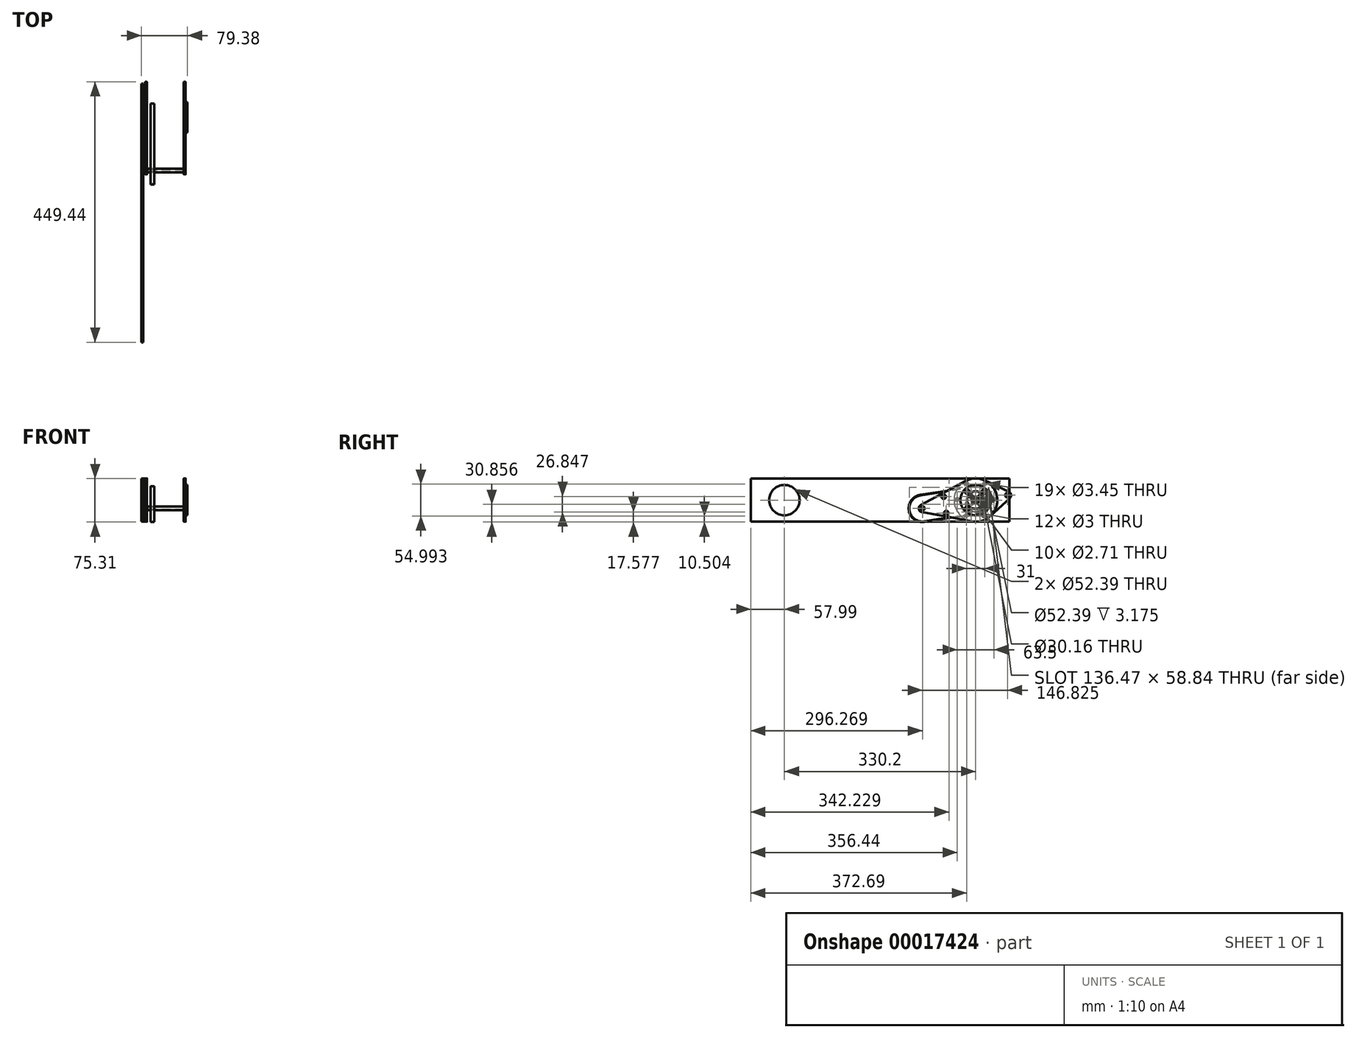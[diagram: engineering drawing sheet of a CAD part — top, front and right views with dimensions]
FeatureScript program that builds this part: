
annotation { "Feature Type Name" : "Feature", "Feature Type Description" : "" }
export const myFeature = defineFeature(function(context is Context, id is Id, definition is map)
    precondition{}
    {
        {
            var Q0;
            Q0=qCreatedBy(makeId("Right.planeOp"),FACE);
            var sketch = newSketch(context, id + "F0", { "sketchPlane" : qUnion([Q0])});
            skCircle(sketch, "E0", {"center": v(0, 0) * mm, "radius": 50.8 * mm, "construction": true});
            skCircle(sketch, "E1", {"center": v(-91.92, -14.29) * mm, "radius": 36.51 * mm, "construction": true});
            skLineSegment(sketch, "E2", {"start": v(0, 0) * mm, "end": v(-91.92, -14.29) * mm, "construction": true});
            skCircle(sketch, "E3", {"center": v(0, -7) * mm, "radius": 18.5 * mm, "construction": true});
            skCircle(sketch, "E4", {"center": v(0, 0) * mm, "radius": 6 * mm});
            skCircle(sketch, "E5", {"center": v(0, 0) * mm, "radius": 26.2 * mm, "construction": true});
            skLineSegment(sketch, "E6", {"start": v(63.5, -50.8) * mm, "end": v(-393.7, -50.8) * mm});
            skLineSegment(sketch, "E7", {"start": v(-165.1, -50.8) * mm, "end": v(-165.1, 406.4) * mm, "construction": true});
            skCircle(sketch, "E8.MirrorC", {"center": v(-238.28, -14.29) * mm, "radius": 36.51 * mm});
            skLineSegment(sketch, "E9.MirrorCS", {"start": v(-330.2, 0) * mm, "end": v(-238.28, -14.29) * mm, "construction": true});
            skCircle(sketch, "E10.MirrorC", {"center": v(-330.2, 0) * mm, "radius": 50.8 * mm});
            skArc(sketch, "E11", {"start": v(-6.86, -36.67) * mm, "mid": v(10.31, -35.85) * mm, "end": v(25.3, -27.42) * mm});
            skArc(sketch, "E12", {"start": v(59.2, 3.87) * mm, "mid": v(61.18, 9.5) * mm, "end": v(57.59, 14.29) * mm});
            skArc(sketch, "E13", {"start": v(-94.93, -8.7) * mm, "mid": v(-98.2, -15.26) * mm, "end": v(-93.09, -20.53) * mm});
            skLineSegment(sketch, "E14", {"start": v(15.78, 33.8) * mm, "end": v(57.59, 14.29) * mm});
            skLineSegment(sketch, "E15", {"start": v(59.2, 3.87) * mm, "end": v(25.3, -27.42) * mm});
            skLineSegment(sketch, "E16", {"start": v(-93.09, -20.53) * mm, "end": v(-6.86, -36.67) * mm});
            skLineSegment(sketch, "E17", {"start": v(-94.93, -8.7) * mm, "end": v(-17.67, 32.86) * mm});
            skArc(sketch, "E18.trimOffspring", {"start": v(15.78, 33.8) * mm, "mid": v(-1.06, 37.3) * mm, "end": v(-17.67, 32.86) * mm});
            skCircle(sketch, "E19", {"center": v(54.9, 8.53) * mm, "radius": 3.18 * mm, "construction": true});
            skCircle(sketch, "E20", {"center": v(-91.92, -14.29) * mm, "radius": 3.18 * mm, "construction": true});
            skSolve(sketch);
        }
        {
            var Q0;
            Q0=makeQuery(id+"F0.imprint","IMPRINT",FACE,{"disambiguationData":[TD([[makeQuery(id+"F0.imprint","IMPRINT",EDGE,{"derivedFrom":sQuery(id+"F0.wireOp",EDGE,"E4")}),-1.0]])]});
            extrude(context, id + "F1", {"entities" : qUnion([Q0]), "depth" : 3.17 * mm});
        }
        {
            var Q0;
            Q0=makeQuery(id+"F0.imprint","IMPRINT",FACE,{"disambiguationData":[TD([[makeQuery(id+"F0.imprint","IMPRINT",EDGE,{"derivedFrom":sQuery(id+"F0.wireOp",EDGE,"E4")}),-1.0]])]});
            var sketch = newSketch(context, id + "F2", { "sketchPlane" : qUnion([Q0])});
            skCircle(sketch, "E21.0", {"center": v(0, 0) * mm, "radius": 26.2 * mm});
            skCircle(sketch, "E22.cCircle", {"center": v(0, 0) * mm, "radius": 20.64 * mm, "construction": true});
            skLineSegment(sketch, "E22.0", {"start": v(-14.6, -14.6) * mm, "end": v(-14.6, 14.6) * mm, "construction": true});
            skLineSegment(sketch, "E22.1", {"start": v(-14.6, 14.6) * mm, "end": v(14.6, 14.6) * mm, "construction": true});
            skLineSegment(sketch, "E22.2", {"start": v(14.6, 14.6) * mm, "end": v(14.6, -14.6) * mm, "construction": true});
            skLineSegment(sketch, "E22.3", {"start": v(14.6, -14.6) * mm, "end": v(-14.6, -14.6) * mm, "construction": true});
            skCircle(sketch, "E23", {"center": v(-14.6, -14.6) * mm, "radius": 3.9 * mm});
            skCircle(sketch, "E24.0", {"center": v(0, 0) * mm, "radius": 6 * mm});
            skSolve(sketch);
        }
        {
            var Q0;
            Q0=makeQuery(id+"F2.imprint","IMPRINT",FACE,{"disambiguationData":[TD([[makeQuery(id+"F2.imprint","IMPRINT",EDGE,{"derivedFrom":sQuery(id+"F2.wireOp",EDGE,"E21.0")}),1.0]])]});
            var Q1;
            Q1=makeQuery(id+"F2.imprint","IMPRINT",FACE,{"disambiguationData":[TD([[makeQuery(id+"F2.imprint","IMPRINT",EDGE,{"derivedFrom":sQuery(id+"F2.wireOp",EDGE,"E23")}),1.0]])]});
            extrude(context, id + "F3", {"entities" : qUnion([Q0, Q1]), "oppositeDirection" : true, "depth" : 3.17 * mm});
        }
        {
            var Q0;
            Q0=makeQuery(id+"F3.opExtrude","CAP_FACE",FACE,{"disambiguationData":[OSD([sQuery(id+"F2.wireOp",EDGE,"E21.0"),sQuery(id+"F2.wireOp",EDGE,"E24.0")])],"isStart":false});
            var sketch = newSketch(context, id + "F4", { "sketchPlane" : qUnion([Q0])});
            skPoint(sketch, "E25.0", {"position": v(14.6, 14.6) * mm});
            skPoint(sketch, "E25.1", {"position": v(-14.6, 14.6) * mm});
            skPoint(sketch, "E25.2", {"position": v(-14.6, -14.6) * mm});
            skPoint(sketch, "E25.3", {"position": v(14.6, -14.6) * mm});
            skSolve(sketch);
        }
        {
            var Q0;
            Q0=sQuery(id+"F4.wireOp",VERTEX,"E25.3");
            var Q1;
            Q1=sQuery(id+"F4.wireOp",VERTEX,"E25.0");
            var Q2;
            Q2=sQuery(id+"F4.wireOp",VERTEX,"E25.1");
            var Q3;
            Q3=sQuery(id+"F4.wireOp",VERTEX,"E25.2");
            var Q4;
            Q4=makeQuery(id+"F3.opExtrude","SWEPT_BODY",BODY,{"disambiguationData":[OSD([sQuery(id+"F2.wireOp",EDGE,"E21.0"),sQuery(id+"F2.wireOp",EDGE,"E24.0")])]});
            hole(context, id + "F5", {"style" : HoleStyle.C_SINK, "holeDiameter" : 3.45 * mm, "cSinkDiameter" : 7.8 * mm, "endStyle" : HoleEndStyle.THROUGH, "locations" : qUnion([Q0, Q1, Q2, Q3]), "scope" : qUnion([Q4]), "cSinkAngle" : 90 * degree});
        }
        {
            var Q0;
            Q0=makeQuery(id+"F1.opExtrude","CAP_FACE",FACE,{"disambiguationData":[OSD([sQuery(id+"F0.wireOp",EDGE,"E4"),sQuery(id+"F0.wireOp",EDGE,"E11"),sQuery(id+"F0.wireOp",EDGE,"E12"),sQuery(id+"F0.wireOp",EDGE,"E13"),sQuery(id+"F0.wireOp",EDGE,"E14"),sQuery(id+"F0.wireOp",EDGE,"E15"),sQuery(id+"F0.wireOp",EDGE,"E16"),sQuery(id+"F0.wireOp",EDGE,"E17"),sQuery(id+"F0.wireOp",EDGE,"E18.trimOffspring")])],"isStart":false});
            var sketch = newSketch(context, id + "F6", { "sketchPlane" : qUnion([Q0])});
            skPoint(sketch, "E26.0", {"position": v(0, -7) * mm});
            skCircle(sketch, "E27.cCircle", {"center": v(0, -7) * mm, "radius": 15.5 * mm, "construction": true});
            skLineSegment(sketch, "E27.0", {"start": v(15.5, -7) * mm, "end": v(7.75, -20.42) * mm});
            skLineSegment(sketch, "E27.1", {"start": v(7.75, -20.42) * mm, "end": v(-7.75, -20.42) * mm});
            skLineSegment(sketch, "E27.2", {"start": v(-7.75, -20.42) * mm, "end": v(-15.5, -7) * mm});
            skLineSegment(sketch, "E27.3", {"start": v(-15.5, -7) * mm, "end": v(-7.75, 6.42) * mm});
            skLineSegment(sketch, "E27.4", {"start": v(-7.75, 6.42) * mm, "end": v(7.75, 6.42) * mm});
            skLineSegment(sketch, "E27.5", {"start": v(7.75, 6.42) * mm, "end": v(15.5, -7) * mm});
            skSolve(sketch);
        }
        {
            var Q0;
            Q0=sQuery(id+"F6.wireOp",VERTEX,"E27.3.end");
            var Q1;
            Q1=sQuery(id+"F6.wireOp",VERTEX,"E27.2.end");
            var Q2;
            Q2=sQuery(id+"F6.wireOp",VERTEX,"E27.2.start");
            var Q3;
            Q3=sQuery(id+"F6.wireOp",VERTEX,"E27.0.end");
            var Q4;
            Q4=sQuery(id+"F6.wireOp",VERTEX,"E27.0.start");
            var Q5;
            Q5=sQuery(id+"F6.wireOp",VERTEX,"E27.4.end");
            var Q6;
            Q6=makeQuery(id+"F1.opExtrude","SWEPT_BODY",BODY,{"disambiguationData":[OSD([sQuery(id+"F0.wireOp",EDGE,"E4"),sQuery(id+"F0.wireOp",EDGE,"E11"),sQuery(id+"F0.wireOp",EDGE,"E12"),sQuery(id+"F0.wireOp",EDGE,"E13"),sQuery(id+"F0.wireOp",EDGE,"E14"),sQuery(id+"F0.wireOp",EDGE,"E15"),sQuery(id+"F0.wireOp",EDGE,"E16"),sQuery(id+"F0.wireOp",EDGE,"E17"),sQuery(id+"F0.wireOp",EDGE,"E18.trimOffspring")])]});
            var Q7;
            Q7=makeQuery(id+"F3.opExtrude","SWEPT_BODY",BODY,{"disambiguationData":[OSD([sQuery(id+"F2.wireOp",EDGE,"E21.0"),sQuery(id+"F2.wireOp",EDGE,"E24.0")])]});
            hole(context, id + "F7", {"style" : HoleStyle.C_SINK, "holeDiameter" : 3 * mm, "cSinkDiameter" : 6 * mm, "endStyle" : HoleEndStyle.THROUGH, "locations" : qUnion([Q0, Q1, Q2, Q3, Q4, Q5]), "scope" : qUnion([Q6, Q7]), "cSinkAngle" : 90 * degree});
        }
        {
            var Q0;
            Q0=makeQuery(id+"F2.imprint","IMPRINT",FACE,{"disambiguationData":[TD([[makeQuery(id+"F2.imprint","IMPRINT",EDGE,{"derivedFrom":sQuery(id+"F2.wireOp",EDGE,"E21.0")}),-1.0]])]});
            var sketch = newSketch(context, id + "F8", { "sketchPlane" : qUnion([Q0])});
            skCircle(sketch, "E28", {"center": v(0, 0) * mm, "radius": 37.3 * mm});
            skCircle(sketch, "E29.cCircle", {"center": v(0, 0) * mm, "radius": 31.75 * mm, "construction": true});
            skLineSegment(sketch, "E29.0", {"start": v(-31.75, 0) * mm, "end": v(-15.88, 27.5) * mm, "construction": true});
            skLineSegment(sketch, "E29.1", {"start": v(-15.87, 27.5) * mm, "end": v(15.87, 27.5) * mm, "construction": true});
            skLineSegment(sketch, "E29.2", {"start": v(15.88, 27.5) * mm, "end": v(31.75, 0) * mm, "construction": true});
            skLineSegment(sketch, "E29.3", {"start": v(31.75, 0) * mm, "end": v(15.87, -27.5) * mm, "construction": true});
            skLineSegment(sketch, "E29.4", {"start": v(15.88, -27.5) * mm, "end": v(-15.88, -27.5) * mm, "construction": true});
            skLineSegment(sketch, "E29.5", {"start": v(-15.88, -27.5) * mm, "end": v(-31.75, 0) * mm, "construction": true});
            skCircle(sketch, "E30", {"center": v(-31.75, 0) * mm, "radius": 3.9 * mm, "construction": true});
            skLineSegment(sketch, "E31", {"start": v(-37.3, 0) * mm, "end": v(-26.2, 0) * mm, "construction": true});
            skCircle(sketch, "E32.1", {"center": v(0, 0) * mm, "radius": 26.2 * mm});
            skSolve(sketch);
        }
        {
            var Q0;
            Q0 = qSketchRegion(id + "F8", true);
            extrude(context, id + "F9", {"entities" : qUnion([Q0]), "oppositeDirection" : true, "depth" : 3.17 * mm});
        }
        {
            var Q0;
            Q0=sQuery(id+"F8.wireOp",VERTEX,"E29.5.end");
            var Q1;
            Q1=sQuery(id+"F8.wireOp",VERTEX,"E29.1.start");
            var Q2;
            Q2=sQuery(id+"F8.wireOp",VERTEX,"E29.2.start");
            var Q3;
            Q3=sQuery(id+"F8.wireOp",VERTEX,"E29.2.end");
            var Q4;
            Q4=sQuery(id+"F8.wireOp",VERTEX,"E29.4.start");
            var Q5;
            Q5=sQuery(id+"F8.wireOp",VERTEX,"E29.5.start");
            var Q6;
            Q6=makeQuery(id+"F9.opExtrude","SWEPT_BODY",BODY,{"disambiguationData":[OSD([sQuery(id+"F8.wireOp",EDGE,"E28"),sQuery(id+"F8.wireOp",EDGE,"E32.1")])]});
            hole(context, id + "F10", {"style" : HoleStyle.C_SINK, "holeDiameter" : 3.45 * mm, "cSinkDiameter" : 7.8 * mm, "endStyle" : HoleEndStyle.THROUGH, "locations" : qUnion([Q0, Q1, Q2, Q3, Q4, Q5]), "scope" : qUnion([Q6]), "cSinkAngle" : 90 * degree});
        }
        {
            var Q0;
            Q0=makeQuery(id+"F1.opExtrude","CAP_FACE",FACE,{"disambiguationData":[OSD([sQuery(id+"F0.wireOp",EDGE,"E4"),sQuery(id+"F0.wireOp",EDGE,"E11"),sQuery(id+"F0.wireOp",EDGE,"E12"),sQuery(id+"F0.wireOp",EDGE,"E13"),sQuery(id+"F0.wireOp",EDGE,"E14"),sQuery(id+"F0.wireOp",EDGE,"E15"),sQuery(id+"F0.wireOp",EDGE,"E16"),sQuery(id+"F0.wireOp",EDGE,"E17"),sQuery(id+"F0.wireOp",EDGE,"E18.trimOffspring")])],"isStart":false});
            cPlane(context, id + "F11", {"entities" : qUnion([Q0]), "cplaneType" : CPlaneType.OFFSET, "offset" : 63.5 * mm, "width" : 152.4 * mm, "height" : 152.4 * mm});
        }
        {
            var Q0;
            Q0=qCreatedBy(id+"F11.planeOp",FACE);
            var sketch = newSketch(context, id + "F12", { "sketchPlane" : qUnion([Q0])});
            skLineSegment(sketch, "E33.0.0", {"start": v(-93.09, -20.53) * mm, "end": v(-6.86, -36.67) * mm});
            skArc(sketch, "E33.0.1", {"start": v(-6.86, -36.67) * mm, "mid": v(10.31, -35.85) * mm, "end": v(25.3, -27.42) * mm});
            skLineSegment(sketch, "E33.0.2", {"start": v(25.3, -27.42) * mm, "end": v(59.2, 3.87) * mm});
            skArc(sketch, "E33.0.3", {"start": v(59.2, 3.87) * mm, "mid": v(61.18, 9.5) * mm, "end": v(57.59, 14.29) * mm});
            skLineSegment(sketch, "E33.0.4", {"start": v(57.59, 14.29) * mm, "end": v(15.78, 33.8) * mm});
            skArc(sketch, "E33.0.5", {"start": v(15.78, 33.8) * mm, "mid": v(-1.06, 37.3) * mm, "end": v(-17.67, 32.86) * mm});
            skLineSegment(sketch, "E33.0.6", {"start": v(-17.67, 32.86) * mm, "end": v(-94.93, -8.7) * mm});
            skArc(sketch, "E33.0.7", {"start": v(-94.93, -8.7) * mm, "mid": v(-98.2, -15.26) * mm, "end": v(-93.09, -20.53) * mm});
            skSolve(sketch);
        }
        {
            var Q0;
            Q0=makeQuery(id+"F12.imprint","IMPRINT",FACE,{"disambiguationData":[TD([[makeQuery(id+"F12.imprint","IMPRINT",EDGE,{"derivedFrom":sQuery(id+"F12.wireOp",EDGE,"E33.0.0")}),1.0]])]});
            extrude(context, id + "F13", {"entities" : qUnion([Q0]), "depth" : 3.17 * mm});
        }
        {
            var Q0;
            Q0=sQuery(id+"F2.wireOp",VERTEX,"E22.1.end");
            var Q1;
            Q1=sQuery(id+"F2.wireOp",VERTEX,"E22.2.end");
            var Q2;
            Q2=sQuery(id+"F2.wireOp",VERTEX,"E22.3.end");
            var Q3;
            Q3=sQuery(id+"F2.wireOp",VERTEX,"E22.0.end");
            var Q4;
            Q4=makeQuery(id+"F1.opExtrude","SWEPT_BODY",BODY,{"disambiguationData":[OSD([sQuery(id+"F0.wireOp",EDGE,"E4"),sQuery(id+"F0.wireOp",EDGE,"E11"),sQuery(id+"F0.wireOp",EDGE,"E12"),sQuery(id+"F0.wireOp",EDGE,"E13"),sQuery(id+"F0.wireOp",EDGE,"E14"),sQuery(id+"F0.wireOp",EDGE,"E15"),sQuery(id+"F0.wireOp",EDGE,"E16"),sQuery(id+"F0.wireOp",EDGE,"E17"),sQuery(id+"F0.wireOp",EDGE,"E18.trimOffspring")])]});
            var Q5;
            Q5=makeQuery(id+"F13.opExtrude","SWEPT_BODY",BODY,{"disambiguationData":[OSD([sQuery(id+"F12.wireOp",EDGE,"E33.0.0"),sQuery(id+"F12.wireOp",EDGE,"E33.0.1"),sQuery(id+"F12.wireOp",EDGE,"E33.0.2"),sQuery(id+"F12.wireOp",EDGE,"E33.0.3"),sQuery(id+"F12.wireOp",EDGE,"E33.0.4"),sQuery(id+"F12.wireOp",EDGE,"E33.0.5"),sQuery(id+"F12.wireOp",EDGE,"E33.0.6"),sQuery(id+"F12.wireOp",EDGE,"E33.0.7")])]});
            hole(context, id + "F14", {"style" : HoleStyle.SIMPLE, "holeDiameter" : 2.7 * mm, "endStyle" : HoleEndStyle.THROUGH, "oppositeDirection" : true, "locations" : qUnion([Q0, Q1, Q2, Q3]), "scope" : qUnion([Q4, Q5])});
        }
        {
            var Q0;
            Q0=makeQuery(id+"F9.opExtrude","CAP_FACE",FACE,{"disambiguationData":[OSD([sQuery(id+"F8.wireOp",EDGE,"E28"),sQuery(id+"F8.wireOp",EDGE,"E32.1")])],"isStart":false});
            var sketch = newSketch(context, id + "F15", { "sketchPlane" : qUnion([Q0])});
            skLineSegment(sketch, "E34.bottom", {"start": v(-57.99, 37.3) * mm, "end": v(388.19, 37.3) * mm});
            skLineSegment(sketch, "E34.top", {"start": v(-57.99, -37.3) * mm, "end": v(388.19, -37.3) * mm});
            skLineSegment(sketch, "E34.left", {"start": v(-57.99, 37.3) * mm, "end": v(-57.99, -37.3) * mm});
            skLineSegment(sketch, "E34.right", {"start": v(388.19, 37.3) * mm, "end": v(388.19, -37.3) * mm});
            skCircle(sketch, "E35.0", {"center": v(0, 0) * mm, "radius": 26.2 * mm});
            skCircle(sketch, "E36", {"center": v(330.2, 0) * mm, "radius": 26.2 * mm});
            skSolve(sketch);
        }
        {
            var Q0;
            Q0 = qSketchRegion(id + "F15", true);
            extrude(context, id + "F16", {"entities" : qUnion([Q0]), "depth" : 3.17 * mm});
        }
        {
            var Q0;
            Q0=sQuery(id+"F8.wireOp",VERTEX,"E29.5.end");
            var Q1;
            Q1=sQuery(id+"F8.wireOp",VERTEX,"E29.0.end");
            var Q2;
            Q2=sQuery(id+"F8.wireOp",VERTEX,"E29.1.end");
            var Q3;
            Q3=sQuery(id+"F8.wireOp",VERTEX,"E29.2.end");
            var Q4;
            Q4=sQuery(id+"F8.wireOp",VERTEX,"E29.4.start");
            var Q5;
            Q5=sQuery(id+"F8.wireOp",VERTEX,"E29.5.start");
            var Q6;
            Q6=makeQuery(id+"F16.opExtrude","SWEPT_BODY",BODY,{"disambiguationData":[OSD([sQuery(id+"F15.wireOp",EDGE,"E34.bottom"),sQuery(id+"F15.wireOp",EDGE,"E34.top"),sQuery(id+"F15.wireOp",EDGE,"E34.left"),sQuery(id+"F15.wireOp",EDGE,"E34.right"),sQuery(id+"F15.wireOp",EDGE,"E35.0"),sQuery(id+"F15.wireOp",EDGE,"E36")])]});
            hole(context, id + "F17", {"style" : HoleStyle.SIMPLE, "holeDiameter" : 2.7 * mm, "endStyle" : HoleEndStyle.THROUGH, "locations" : qUnion([Q0, Q1, Q2, Q3, Q4, Q5]), "scope" : qUnion([Q6])});
        }
        {
            var Q0;
            Q0=makeQuery(id+"F1.opExtrude","CAP_FACE",FACE,{"disambiguationData":[OSD([sQuery(id+"F0.wireOp",EDGE,"E4"),sQuery(id+"F0.wireOp",EDGE,"E11"),sQuery(id+"F0.wireOp",EDGE,"E12"),sQuery(id+"F0.wireOp",EDGE,"E13"),sQuery(id+"F0.wireOp",EDGE,"E14"),sQuery(id+"F0.wireOp",EDGE,"E15"),sQuery(id+"F0.wireOp",EDGE,"E16"),sQuery(id+"F0.wireOp",EDGE,"E17"),sQuery(id+"F0.wireOp",EDGE,"E18.trimOffspring")])],"isStart":false});
            cPlane(context, id + "F18", {"entities" : qUnion([Q0]), "cplaneType" : CPlaneType.OFFSET, "offset" : 6.35 * mm, "width" : 152.4 * mm, "height" : 152.4 * mm});
        }
        {
            var Q0;
            Q0=qCreatedBy(id+"F18.planeOp",FACE);
            var sketch = newSketch(context, id + "F19", { "sketchPlane" : qUnion([Q0])});
            skPoint(sketch, "E37.0", {"position": v(-91.92, -14.29) * mm});
            skArc(sketch, "E38", {"start": v(-95.38, 7.99) * mm, "mid": v(-114.2, -17.75) * mm, "end": v(-88.46, -36.56) * mm});
            skArc(sketch, "E39", {"start": v(3.46, -22.28) * mm, "mid": v(22.28, 3.46) * mm, "end": v(-3.46, 22.28) * mm});
            skLineSegment(sketch, "E40", {"start": v(-3.46, 22.28) * mm, "end": v(-95.38, 7.99) * mm});
            skLineSegment(sketch, "E41", {"start": v(-88.46, -36.56) * mm, "end": v(3.46, -22.28) * mm});
            skLineSegment(sketch, "E42.0", {"start": v(-3.64, 23.43) * mm, "end": v(-95.56, 9.14) * mm});
            skArc(sketch, "E42.1", {"start": v(3.64, -23.43) * mm, "mid": v(23.43, 3.64) * mm, "end": v(-3.64, 23.43) * mm});
            skLineSegment(sketch, "E42.2", {"start": v(-88.28, -37.72) * mm, "end": v(3.64, -23.43) * mm});
            skArc(sketch, "E42.3", {"start": v(-95.56, 9.14) * mm, "mid": v(-115.35, -17.93) * mm, "end": v(-88.28, -37.72) * mm});
            skSolve(sketch);
        }
        {
            var Q0;
            Q0 = qSketchRegion(id + "F19", true);
            extrude(context, id + "F20", {"entities" : qUnion([Q0]), "depth" : 6 * mm});
        }
        {
            var Q0;
            Q0=makeQuery(id+"F1.opExtrude","CAP_FACE",FACE,{"disambiguationData":[OSD([sQuery(id+"F0.wireOp",EDGE,"E4"),sQuery(id+"F0.wireOp",EDGE,"E11"),sQuery(id+"F0.wireOp",EDGE,"E12"),sQuery(id+"F0.wireOp",EDGE,"E13"),sQuery(id+"F0.wireOp",EDGE,"E14"),sQuery(id+"F0.wireOp",EDGE,"E15"),sQuery(id+"F0.wireOp",EDGE,"E16"),sQuery(id+"F0.wireOp",EDGE,"E17"),sQuery(id+"F0.wireOp",EDGE,"E18.trimOffspring")])],"isStart":false});
            var sketch = newSketch(context, id + "F21", { "sketchPlane" : qUnion([Q0])});
            skCircle(sketch, "E43", {"center": v(-91.92, -14.29) * mm, "radius": 3.18 * mm});
            skSolve(sketch);
        }
        {
            var Q0;
            Q0 = qSketchRegion(id + "F21", true);
            var Q1;
            Q1=makeQuery(id+"F13.opExtrude","CAP_FACE",FACE,{"disambiguationData":[OSD([sQuery(id+"F12.wireOp",EDGE,"E33.0.0"),sQuery(id+"F12.wireOp",EDGE,"E33.0.1"),sQuery(id+"F12.wireOp",EDGE,"E33.0.2"),sQuery(id+"F12.wireOp",EDGE,"E33.0.3"),sQuery(id+"F12.wireOp",EDGE,"E33.0.4"),sQuery(id+"F12.wireOp",EDGE,"E33.0.5"),sQuery(id+"F12.wireOp",EDGE,"E33.0.6"),sQuery(id+"F12.wireOp",EDGE,"E33.0.7")])],"isStart":true});
            extrude(context, id + "F22", {"entities" : qUnion([Q0]), "endBound" : BoundingType.UP_TO_SURFACE, "endBoundEntityFace" : qUnion([Q1]), "depth" : 25.4 * mm});
        }
        {
            var Q0;
            Q0=makeQuery(id+"F8.imprint","IMPRINT",FACE,{"disambiguationData":[TD([[makeQuery(id+"F8.imprint","IMPRINT",EDGE,{"derivedFrom":makeQuery(id+"F2.imprint","IMPRINT",EDGE,{"derivedFrom":makeQuery(id+"F0.imprint","IMPRINT",EDGE,{"derivedFrom":sQuery(id+"F0.wireOp",EDGE,"E13")})})}),1.0]])]});
            var sketch = newSketch(context, id + "F23", { "sketchPlane" : qUnion([Q0])});
            skLineSegment(sketch, "E44", {"start": v(-50.2, -7.8) * mm, "end": v(-55.84, -8.68) * mm});
            skLineSegment(sketch, "E45", {"start": v(-50.83, -22.36) * mm, "end": v(-55.21, 5.88) * mm});
            skCircle(sketch, "E46", {"center": v(-55.21, 5.88) * mm, "radius": 3.18 * mm});
            skCircle(sketch, "E47", {"center": v(-50.83, -22.36) * mm, "radius": 3.18 * mm});
            skPoint(sketch, "E48", {"position": v(-53.02, -8.24) * mm});
            skSolve(sketch);
        }
        {
            var Q0;
            Q0=sQuery(id+"F0.wireOp",VERTEX,"E1.center");
            var Q1;
            Q1=sQuery(id+"F0.wireOp",VERTEX,"E12.center");
            var Q2;
            Q2=sQuery(id+"F23.wireOp",VERTEX,"E45.start");
            var Q3;
            Q3=sQuery(id+"F23.wireOp",VERTEX,"E45.end");
            var Q4;
            Q4=makeQuery(id+"F1.opExtrude","SWEPT_BODY",BODY,{"disambiguationData":[OSD([sQuery(id+"F0.wireOp",EDGE,"E4"),sQuery(id+"F0.wireOp",EDGE,"E11"),sQuery(id+"F0.wireOp",EDGE,"E12"),sQuery(id+"F0.wireOp",EDGE,"E13"),sQuery(id+"F0.wireOp",EDGE,"E14"),sQuery(id+"F0.wireOp",EDGE,"E15"),sQuery(id+"F0.wireOp",EDGE,"E16"),sQuery(id+"F0.wireOp",EDGE,"E17"),sQuery(id+"F0.wireOp",EDGE,"E18.trimOffspring")])]});
            var Q5;
            Q5=makeQuery(id+"F22.opExtrude","SWEPT_BODY",BODY,{"disambiguationData":[OSD([sQuery(id+"F21.wireOp",EDGE,"E43")])]});
            var Q6;
            Q6=makeQuery(id+"F13.opExtrude","SWEPT_BODY",BODY,{"disambiguationData":[OSD([sQuery(id+"F12.wireOp",EDGE,"E33.0.0"),sQuery(id+"F12.wireOp",EDGE,"E33.0.1"),sQuery(id+"F12.wireOp",EDGE,"E33.0.2"),sQuery(id+"F12.wireOp",EDGE,"E33.0.3"),sQuery(id+"F12.wireOp",EDGE,"E33.0.4"),sQuery(id+"F12.wireOp",EDGE,"E33.0.5"),sQuery(id+"F12.wireOp",EDGE,"E33.0.6"),sQuery(id+"F12.wireOp",EDGE,"E33.0.7")])]});
            hole(context, id + "F24", {"style" : HoleStyle.C_SINK, "holeDiameter" : 3.45 * mm, "cSinkDiameter" : 7.8 * mm, "endStyle" : HoleEndStyle.THROUGH, "oppositeDirection" : true, "locations" : qUnion([Q0, Q1, Q2, Q3]), "scope" : qUnion([Q4, Q5, Q6]), "cSinkAngle" : 90 * degree});
        }
        {
            var Q0;
            Q0=makeQuery(id+"F22.opExtrude","SWEPT_FACE",FACE,{"disambiguationData":[OSD([sQuery(id+"F21.wireOp",EDGE,"E43")])]});
            var Q1;
            Q1=makeQuery(id+"F24.hole-0.boolean.opBoolean","COPY",FACE,{"disambiguationData":[OD(2.0)],"derivedFrom":makeQuery(id+"F24.hole-0.opRevolve","SWEPT_FACE",FACE,{"disambiguationData":[OSD([sQuery(id+"F24.hole-0.sketch.wireOp",EDGE,"core_line_2")])]})});
            chamfer(context, id + "F25", {"entities" : qUnion([Q0, Q1]), "width" : 0.25 * mm, "tangentPropagation" : true});
        }
        {
            var Q0;
            Q0=makeQuery(id+"F13.opExtrude","CAP_FACE",FACE,{"disambiguationData":[OSD([sQuery(id+"F12.wireOp",EDGE,"E33.0.0"),sQuery(id+"F12.wireOp",EDGE,"E33.0.1"),sQuery(id+"F12.wireOp",EDGE,"E33.0.2"),sQuery(id+"F12.wireOp",EDGE,"E33.0.3"),sQuery(id+"F12.wireOp",EDGE,"E33.0.4"),sQuery(id+"F12.wireOp",EDGE,"E33.0.5"),sQuery(id+"F12.wireOp",EDGE,"E33.0.6"),sQuery(id+"F12.wireOp",EDGE,"E33.0.7")])],"isStart":false});
            var sketch = newSketch(context, id + "F26", { "sketchPlane" : qUnion([Q0])});
            skPoint(sketch, "E49", {"position": v(-91.92, -14.29) * mm});
            skPoint(sketch, "E50", {"position": v(-55.21, 5.88) * mm});
            skPoint(sketch, "E51", {"position": v(-50.83, -22.36) * mm});
            skPoint(sketch, "E52", {"position": v(54.9, 8.53) * mm});
            skSolve(sketch);
        }
        {
            var Q0;
            Q0=sQuery(id+"F26.wireOp",VERTEX,"E49");
            var Q1;
            Q1=sQuery(id+"F26.wireOp",VERTEX,"E50");
            var Q2;
            Q2=sQuery(id+"F26.wireOp",VERTEX,"E51");
            var Q3;
            Q3=sQuery(id+"F26.wireOp",VERTEX,"E52");
            var Q4;
            Q4=makeQuery(id+"F13.opExtrude","SWEPT_BODY",BODY,{"disambiguationData":[OSD([sQuery(id+"F12.wireOp",EDGE,"E33.0.0"),sQuery(id+"F12.wireOp",EDGE,"E33.0.1"),sQuery(id+"F12.wireOp",EDGE,"E33.0.2"),sQuery(id+"F12.wireOp",EDGE,"E33.0.3"),sQuery(id+"F12.wireOp",EDGE,"E33.0.4"),sQuery(id+"F12.wireOp",EDGE,"E33.0.5"),sQuery(id+"F12.wireOp",EDGE,"E33.0.6"),sQuery(id+"F12.wireOp",EDGE,"E33.0.7")])]});
            hole(context, id + "F27", {"style" : HoleStyle.C_SINK, "holeDiameter" : 3.45 * mm, "cSinkDiameter" : 7.8 * mm, "endStyle" : HoleEndStyle.THROUGH, "locations" : qUnion([Q0, Q1, Q2, Q3]), "scope" : qUnion([Q4]), "cSinkAngle" : 90 * degree});
        }
        {
            var Q0;
            Q0=makeQuery(id+"F1.opExtrude","CAP_FACE",FACE,{"disambiguationData":[OSD([sQuery(id+"F0.wireOp",EDGE,"E4"),sQuery(id+"F0.wireOp",EDGE,"E11"),sQuery(id+"F0.wireOp",EDGE,"E12"),sQuery(id+"F0.wireOp",EDGE,"E13"),sQuery(id+"F0.wireOp",EDGE,"E14"),sQuery(id+"F0.wireOp",EDGE,"E15"),sQuery(id+"F0.wireOp",EDGE,"E16"),sQuery(id+"F0.wireOp",EDGE,"E17"),sQuery(id+"F0.wireOp",EDGE,"E18.trimOffspring")])],"isStart":false});
            var Q1;
            Q1=makeQuery(id+"F13.opExtrude","CAP_FACE",FACE,{"disambiguationData":[OSD([sQuery(id+"F12.wireOp",EDGE,"E33.0.0"),sQuery(id+"F12.wireOp",EDGE,"E33.0.1"),sQuery(id+"F12.wireOp",EDGE,"E33.0.2"),sQuery(id+"F12.wireOp",EDGE,"E33.0.3"),sQuery(id+"F12.wireOp",EDGE,"E33.0.4"),sQuery(id+"F12.wireOp",EDGE,"E33.0.5"),sQuery(id+"F12.wireOp",EDGE,"E33.0.6"),sQuery(id+"F12.wireOp",EDGE,"E33.0.7")])],"isStart":true});
            cPlane(context, id + "F28", {"entities" : qUnion([Q0, Q1]), "cplaneType" : CPlaneType.MID_PLANE, "offset" : 152.4 * mm, "width" : 152.4 * mm, "height" : 152.4 * mm});
        }
        {
            var Q0;
            Q0=makeQuery(id+"F3.opExtrude","SWEPT_BODY",BODY,{"disambiguationData":[OSD([sQuery(id+"F2.wireOp",EDGE,"E21.0"),sQuery(id+"F2.wireOp",EDGE,"E24.0")])]});
            var Q1;
            Q1=qCreatedBy(id+"F28.planeOp",FACE);
            mirror(context, id + "F29", {"entities" : qUnion([Q0]), "mirrorPlane" : qUnion([Q1])});
        }
        {
            var Q0;
            Q0=makeQuery(id+"F29.opPattern","COPY",FACE,{"derivedFrom":makeQuery(id+"F3.opExtrude","CAP_FACE",FACE,{"disambiguationData":[OSD([sQuery(id+"F2.wireOp",EDGE,"E21.0"),sQuery(id+"F2.wireOp",EDGE,"E24.0")])],"isStart":false}),"instanceName":"1"});
            var sketch = newSketch(context, id + "F30", { "sketchPlane" : qUnion([Q0])});
            skCircle(sketch, "E53.0", {"center": v(7.75, 6.42) * mm, "radius": 1.5 * mm});
            skCircle(sketch, "E53.1", {"center": v(0, 0) * mm, "radius": 6 * mm});
            skCircle(sketch, "E53.2", {"center": v(15.5, -7) * mm, "radius": 1.5 * mm});
            skCircle(sketch, "E53.3", {"center": v(7.75, -20.42) * mm, "radius": 1.5 * mm});
            skCircle(sketch, "E53.4", {"center": v(-7.75, -20.42) * mm, "radius": 1.5 * mm});
            skCircle(sketch, "E53.5", {"center": v(-15.5, -7) * mm, "radius": 1.5 * mm});
            skCircle(sketch, "E53.6", {"center": v(-7.75, 6.42) * mm, "radius": 1.5 * mm});
            skCircle(sketch, "E54", {"center": v(0, 0) * mm, "radius": 15.08 * mm});
            skCircle(sketch, "E55.0", {"center": v(14.6, 14.6) * mm, "radius": 1.73 * mm});
            skLineSegment(sketch, "E56", {"start": v(18.52, 18.52) * mm, "end": v(10.66, 10.66) * mm});
            skSolve(sketch);
        }
        {
            var Q0;
            Q0=makeQuery(id+"F30.imprint","IMPRINT",FACE,{"disambiguationData":[TD([[makeQuery(id+"F30.imprint","IMPRINT",EDGE,{"derivedFrom":sQuery(id+"F30.wireOp",EDGE,"E53.6")}),-1.0]])]});
            var Q1;
            Q1=makeQuery(id+"F30.imprint","IMPRINT",FACE,{"disambiguationData":[TD([[makeQuery(id+"F30.imprint","IMPRINT",EDGE,{"derivedFrom":sQuery(id+"F30.wireOp",EDGE,"E53.1")}),1.0]])]});
            var Q2;
            Q2=makeQuery(id+"F30.imprint","IMPRINT",FACE,{"disambiguationData":[TD([[makeQuery(id+"F30.imprint","IMPRINT",EDGE,{"derivedFrom":sQuery(id+"F30.wireOp",EDGE,"E53.0")}),-1.0]])]});
            var Q3;
            Q3=makeQuery(id+"F30.imprint","IMPRINT",FACE,{"disambiguationData":[TD([[makeQuery(id+"F30.imprint","IMPRINT",EDGE,{"derivedFrom":sQuery(id+"F30.wireOp",EDGE,"E53.2")}),-1.0]])]});
            var Q4;
            Q4=makeQuery(id+"F30.imprint","IMPRINT",FACE,{"disambiguationData":[TD([[makeQuery(id+"F30.imprint","IMPRINT",EDGE,{"derivedFrom":sQuery(id+"F30.wireOp",EDGE,"E53.3")}),-1.0]])]});
            var Q5;
            Q5=makeQuery(id+"F30.imprint","IMPRINT",FACE,{"disambiguationData":[TD([[makeQuery(id+"F30.imprint","IMPRINT",EDGE,{"derivedFrom":sQuery(id+"F30.wireOp",EDGE,"E53.4")}),-1.0]])]});
            var Q6;
            Q6=makeQuery(id+"F30.imprint","IMPRINT",FACE,{"disambiguationData":[TD([[makeQuery(id+"F30.imprint","IMPRINT",EDGE,{"derivedFrom":sQuery(id+"F30.wireOp",EDGE,"E53.5")}),-1.0]])]});
            extrude(context, id + "F31", {"entities" : qUnion([Q0, Q1, Q2, Q3, Q4, Q5, Q6]), "operationType" : NewBodyOperationType.ADD, "endBound" : BoundingType.UP_TO_NEXT, "oppositeDirection" : true, "depth" : 25.4 * mm});
        }
        {
            var Q0;
            Q0=makeQuery(id+"F30.imprint","IMPRINT",FACE,{"disambiguationData":[TD([[makeQuery(id+"F30.imprint","IMPRINT",EDGE,{"derivedFrom":sQuery(id+"F30.wireOp",EDGE,"E53.0")}),1.0]])]});
            var Q1;
            Q1=makeQuery(id+"F30.imprint","IMPRINT",FACE,{"disambiguationData":[TD([[makeQuery(id+"F30.imprint","IMPRINT",EDGE,{"derivedFrom":sQuery(id+"F30.wireOp",EDGE,"E53.6")}),-1.0]])]});
            var Q2;
            Q2=makeQuery(id+"F30.imprint","IMPRINT",FACE,{"disambiguationData":[TD([[makeQuery(id+"F30.imprint","IMPRINT",EDGE,{"derivedFrom":sQuery(id+"F30.wireOp",EDGE,"E53.0")}),-1.0]])]});
            var Q3;
            Q3=makeQuery(id+"F30.imprint","IMPRINT",FACE,{"disambiguationData":[TD([[makeQuery(id+"F30.imprint","IMPRINT",EDGE,{"derivedFrom":sQuery(id+"F30.wireOp",EDGE,"E53.1")}),1.0]])]});
            extrude(context, id + "F32", {"entities" : qUnion([Q0, Q1, Q2, Q3]), "operationType" : NewBodyOperationType.REMOVE, "endBound" : BoundingType.UP_TO_NEXT, "oppositeDirection" : true, "depth" : 25.4 * mm});
        }
    });
